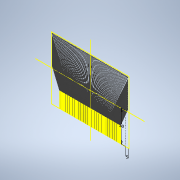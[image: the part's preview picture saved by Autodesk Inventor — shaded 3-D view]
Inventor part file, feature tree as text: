
AUTODESK INVENTOR PART (.ipt)
format: ipt  version: 2021 (Build 250183000, 183)  size: 3,247,616 bytes
history: native  units: in
note: dims shown in document units (in); Inventor stores cm internally (conversion verified against a paired STEP export)
features: sketch x7, extrude x6, projected_geometry x5, pattern_linear x3, mirror x2
ambient origin geometry x8: Origin, YZ Plane, XZ Plane, XY Plane, X Axis, Y Axis, Z Axis, Center Point
bodies: Solid1 (feature_tree)
feature tree (23):
  extrude  "Extrusion1"  Depth=3.1496in
  extrude  "Extrusion2"  Depth=0.0118in
  pattern_linear  "Rectangular Pattern1"  Count1=2  [1 undecoded]
  sketch  "Sketch3"  dims[d6=0.0014in d7=0.0in d8=51.5748in d10=0.0236in d11=1.5748in]
  extrude  "Extrusion3"  Depth=0.0236in
  pattern_linear  "Rectangular Pattern2"  Count1=4  [1 undecoded]
  extrude  "Extrusion4"  Depth=0.0394in
  pattern_linear  "Rectangular Pattern3"  Count1=77 Spacing1=0.05in
  mirror  "Mirror1"
  extrude  "Extrusion5"  Depth=0.0591in
  mirror  "Mirror2"
  extrude  "Extrusion6"  Depth=0.0014in
  sketch  "Sketch1"  dims[d0=3.937in d1=3.1496in]
  sketch  "Sketch2"  dims[d2=0.0394in d3=0.0in d4=0.0118in d5=0.7874in]
  projected_geometry  "Projected Loop1"
  projected_geometry  "Projected Loop2"
  sketch  "Sketch4"  dims[d12=0.1969in d13=0.0394in]
  projected_geometry  "Projected Loop3"
  sketch  "Sketch5"  dims[d14=0.0591in]
  projected_geometry  "Projected Loop4"
  sketch  "Sketch7"  dims[d15=0.0014in d16=0.0in d17=30.315in d19=0.05in d20=0.3937in d22=0.05in]
  projected_geometry  "Projected Loop6"
  sketch  "Sketch8"  dims[d23=0.0157in d24=0.0591in d25=0.1083in d26=0.0014in d27=0.0in d28=10.6299in d30=0.05in d35=0.0118in d36=0.0118in d37=0.0118in d38=0.0118in d39=0.0118in d40=0.0118in d41=0.0118in d42=0.0118in d43=0.0118in d44=0.0118in d45=0.0118in d46=0.0118in d47=0.0118in d48=0.0118in d49=0.0118in d50=0.0118in d51=0.0118in d52=0.0118in d53=0.0118in d54=0.0118in d55=0.0118in d56=0.0118in d57=0.0118in d58=0.0118in d59=0.0118in d60=0.0118in d61=0.0118in d62=0.0118in d63=0.0118in d64=0.0118in d65=0.0118in d66=0.0118in d67=0.0118in d68=0.0118in d69=0.0118in d70=0.0118in d71=0.0118in d72=0.0118in d73=0.0118in d74=0.0118in d75=0.0118in d76=0.0118in d77=0.0118in d78=0.0118in d79=0.0118in d80=0.0118in d81=0.0118in d82=0.0118in d83=0.0118in d84=0.0118in d85=0.0118in d86=0.0118in d87=0.0118in d88=0.0118in d89=0.0118in d90=0.0118in d91=0.0118in d92=0.0118in d93=0.0118in d94=0.0118in d95=0.0118in d96=0.0118in d97=0.0118in d98=0.0118in d99=0.0118in d100=0.0118in d101=0.0014in d102=0.0in d103=0.0014in d104=0.0in]
note: 2 required parameter values undecoded (feature->parameter linkage not recoverable at this tier; creation-order binding heuristic only, values carry confidence <= 0.55)
